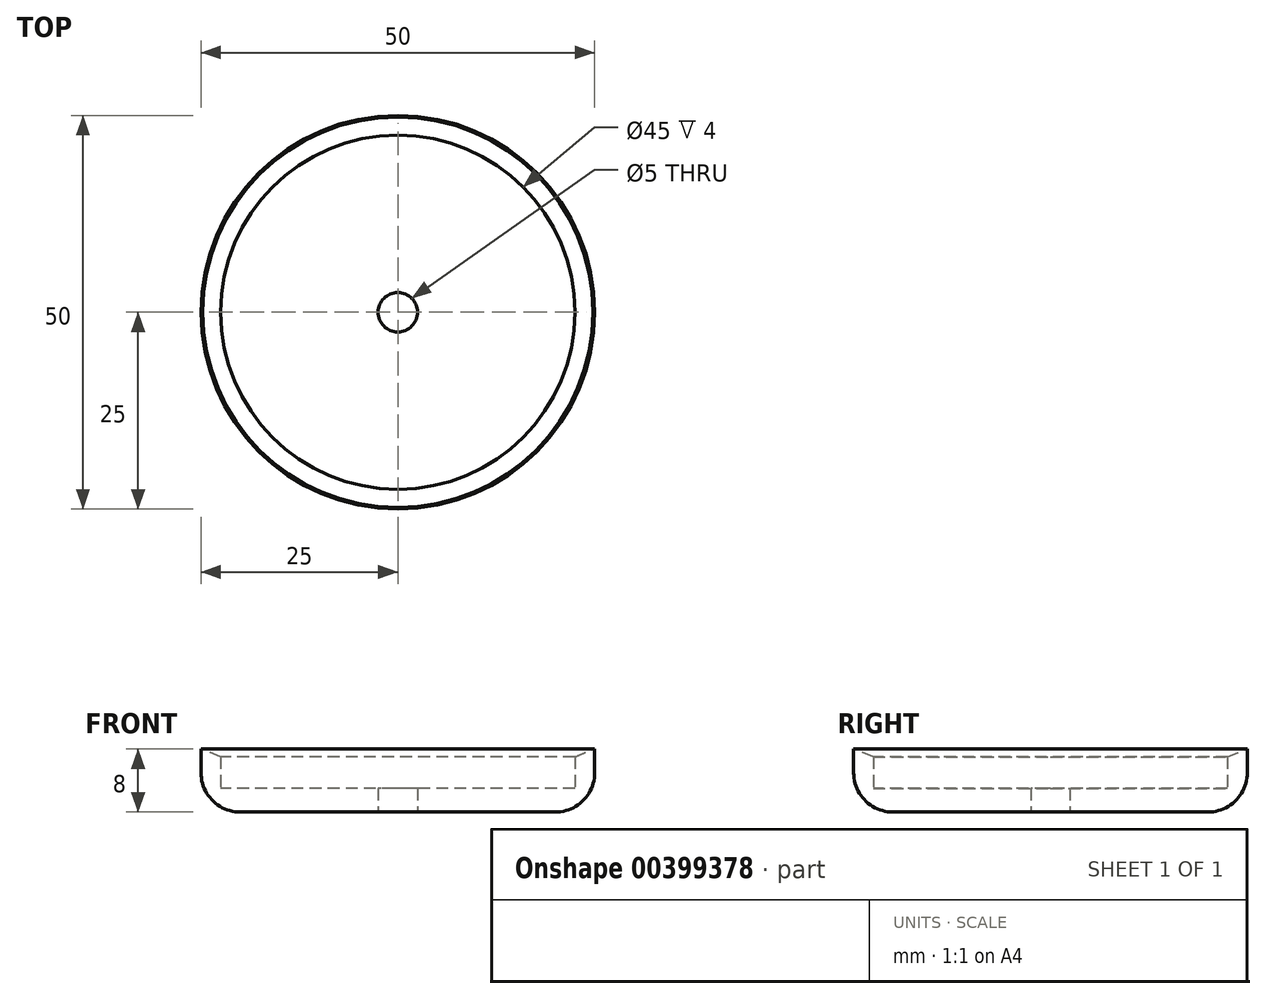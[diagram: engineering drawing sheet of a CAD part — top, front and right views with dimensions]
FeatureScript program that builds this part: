
annotation { "Feature Type Name" : "Feature", "Feature Type Description" : "" }
export const myFeature = defineFeature(function(context is Context, id is Id, definition is map)
    precondition{}
    {
        {
            var Q0;
            Q0=qCreatedBy(makeId("Top.planeOp"),FACE);
            var sketch = newSketch(context, id + "F0", { "sketchPlane" : qUnion([Q0])});
            skCircle(sketch, "E0", {"center": v(0, 0) * mm, "radius": 25 * mm});
            skCircle(sketch, "E1", {"center": v(0, 0) * mm, "radius": 22.5 * mm});
            skSolve(sketch);
        }
        {
            var Q0;
            Q0=makeQuery(id+"F0.imprint","IMPRINT",FACE,{"disambiguationData":[TD([[makeQuery(id+"F0.imprint","IMPRINT",EDGE,{"derivedFrom":sQuery(id+"F0.wireOp",EDGE,"E1")}),1.0]])]});
            extrude(context, id + "F1", {"entities" : qUnion([Q0]), "depth" : 3 * mm});
        }
        {
            var Q0;
            Q0=makeQuery(id+"F0.imprint","IMPRINT",FACE,{"disambiguationData":[TD([[makeQuery(id+"F0.imprint","IMPRINT",EDGE,{"derivedFrom":sQuery(id+"F0.wireOp",EDGE,"E0")}),1.0]])]});
            extrude(context, id + "F2", {"entities" : qUnion([Q0]), "operationType" : NewBodyOperationType.ADD, "depth" : 8 * mm});
        }
        {
            var Q0;
            Q0=makeQuery(id+"F2.opExtrude","CAP_EDGE",EDGE,{"disambiguationData":[OSD([sQuery(id+"F0.wireOp",EDGE,"E0")])],"isStart":true});
            fillet(context, id + "F3", {"entities" : qUnion([Q0]), "radius" : 5 * mm, "tangentPropagation" : true, "allowEdgeOverflow" : false});
        }
        {
            var Q0;
            Q0=makeQuery(id+"F2.opExtrude","CAP_EDGE",EDGE,{"disambiguationData":[OSD([sQuery(id+"F0.wireOp",EDGE,"E1")])],"isStart":false});
            chamfer(context, id + "F4", {"entities" : qUnion([Q0]), "chamferType" : ChamferType.TWO_OFFSETS, "width1" : 1 * mm, "oppositeDirection" : false, "width2" : 2.3 * mm, "tangentPropagation" : true});
        }
        {
            var Q0;
            Q0=sQuery(id+"F0.wireOp",VERTEX,"E0.center");
            var Q1;
            Q1=makeQuery(id+"F1.opExtrude","SWEPT_BODY",BODY,{"disambiguationData":[OSD([sQuery(id+"F0.wireOp",EDGE,"E1")])]});
            hole(context, id + "F5", {"style" : HoleStyle.SIMPLE, "endStyle" : HoleEndStyle.THROUGH, "oppositeDirection" : true, "holeDiameter" : 5 * mm, "isTappedThrough" : true, "tappedDepth" : 12 * mm, "tapClearance" : 3, "locations" : qUnion([Q0]), "scope" : qUnion([Q1])});
        }
    });
